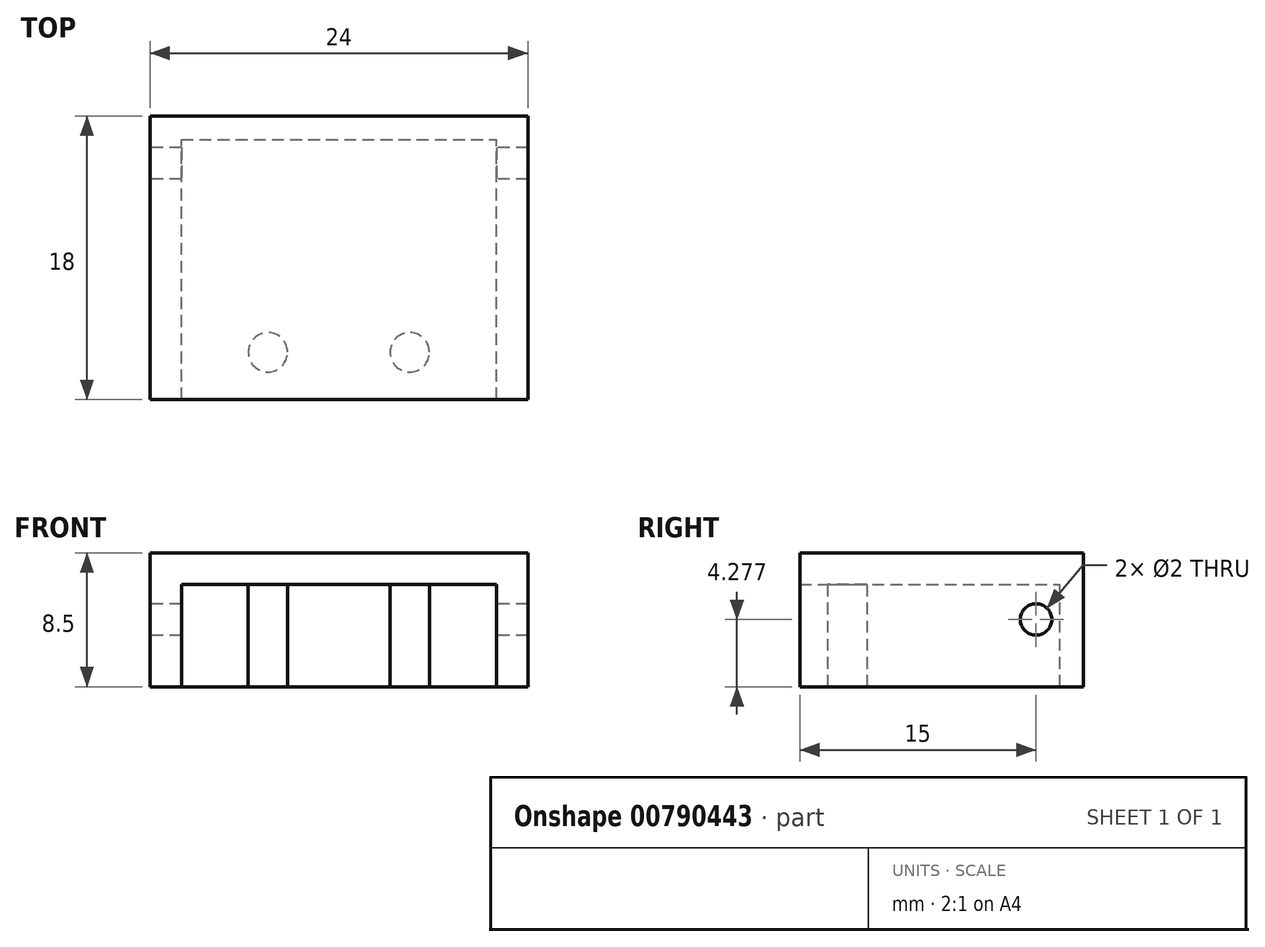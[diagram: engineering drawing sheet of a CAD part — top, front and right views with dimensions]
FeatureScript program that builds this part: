
annotation { "Feature Type Name" : "Feature", "Feature Type Description" : "" }
export const myFeature = defineFeature(function(context is Context, id is Id, definition is map)
    precondition{}
    {
        {
            var Q0;
            Q0=qCreatedBy(makeId("Top.planeOp"),FACE);
            var sketch = newSketch(context, id + "F0", { "sketchPlane" : qUnion([Q0])});
            skLineSegment(sketch, "E0.bottom", {"start": v(-12, -6) * mm, "end": v(12, -6) * mm});
            skLineSegment(sketch, "E0.top", {"start": v(-12, 12) * mm, "end": v(12, 12) * mm});
            skLineSegment(sketch, "E0.left", {"start": v(-12, -6) * mm, "end": v(-12, 12) * mm});
            skLineSegment(sketch, "E0.right", {"start": v(12, -6) * mm, "end": v(12, 12) * mm});
            skSolve(sketch);
        }
        {
            var Q0;
            Q0=qCreatedBy(makeId("Top.planeOp"),FACE);
            var sketch = newSketch(context, id + "F1", { "sketchPlane" : qUnion([Q0])});
            skLineSegment(sketch, "E1.bottom", {"start": v(-10, -6) * mm, "end": v(10, -6) * mm});
            skLineSegment(sketch, "E1.top", {"start": v(-10, 6) * mm, "end": v(10, 6) * mm});
            skLineSegment(sketch, "E1.left", {"start": v(-10, -6) * mm, "end": v(-10, 6) * mm});
            skLineSegment(sketch, "E1.right", {"start": v(10, -6) * mm, "end": v(10, 6) * mm});
            skCircle(sketch, "E2", {"center": v(-4.5, -3) * mm, "radius": 1.25 * mm});
            skCircle(sketch, "E3", {"center": v(4.5, -3) * mm, "radius": 1.25 * mm});
            skSolve(sketch);
        }
        {
            var Q0;
            Q0=makeQuery(id+"F0.imprint","IMPRINT",FACE,{"disambiguationData":[TD([[makeQuery(id+"F0.imprint","IMPRINT",EDGE,{"derivedFrom":sQuery(id+"F0.wireOp",EDGE,"E0.bottom")}),1.0]])]});
            extrude(context, id + "F2", {"entities" : qUnion([Q0]), "depth" : 8.5 * mm, "offsetDistance" : 25 * mm});
        }
        {
            var Q0;
            Q0 = qSketchRegion(id + "F1", true);
            extrude(context, id + "F3", {"entities" : qUnion([Q0]), "operationType" : NewBodyOperationType.REMOVE, "depth" : 6.5 * mm, "offsetDistance" : 25 * mm});
        }
        {
            var Q0;
            Q0=makeQuery(id+"F2.opExtrude","SWEPT_FACE",FACE,{"disambiguationData":[OSD([sQuery(id+"F0.wireOp",EDGE,"E0.left")])]});
            var sketch = newSketch(context, id + "F4", { "sketchPlane" : qUnion([Q0])});
            skCircle(sketch, "E4", {"center": v(-9, 4.28) * mm, "radius": 1 * mm});
            skSolve(sketch);
        }
        {
            var Q0;
            Q0 = qSketchRegion(id + "F4", true);
            var Q1;
            Q1=makeQuery(id+"F4.imprint","IMPRINT",FACE,{"disambiguationData":[TD([[makeQuery(id+"F4.imprint","IMPRINT",EDGE,{"derivedFrom":sQuery(id+"F4.wireOp",EDGE,"E4")}),1.0]])]});
            extrude(context, id + "F5", {"entities" : qUnion([Q0, Q1]), "operationType" : NewBodyOperationType.REMOVE, "oppositeDirection" : true, "depth" : 25 * mm, "offsetDistance" : 25 * mm});
        }
        {
            var Q0;
            Q0=makeQuery(id+"F3.boolean.opBoolean","COPY",FACE,{"derivedFrom":makeQuery(id+"F3.opExtrude","SWEPT_FACE",FACE,{"disambiguationData":[OSD([sQuery(id+"F1.wireOp",EDGE,"E1.top")])]})});
            extrude(context, id + "F6", {"entities" : qUnion([Q0]), "operationType" : NewBodyOperationType.REMOVE, "oppositeDirection" : true, "depth" : 4.5 * mm, "offsetDistance" : 25 * mm});
        }
    });
